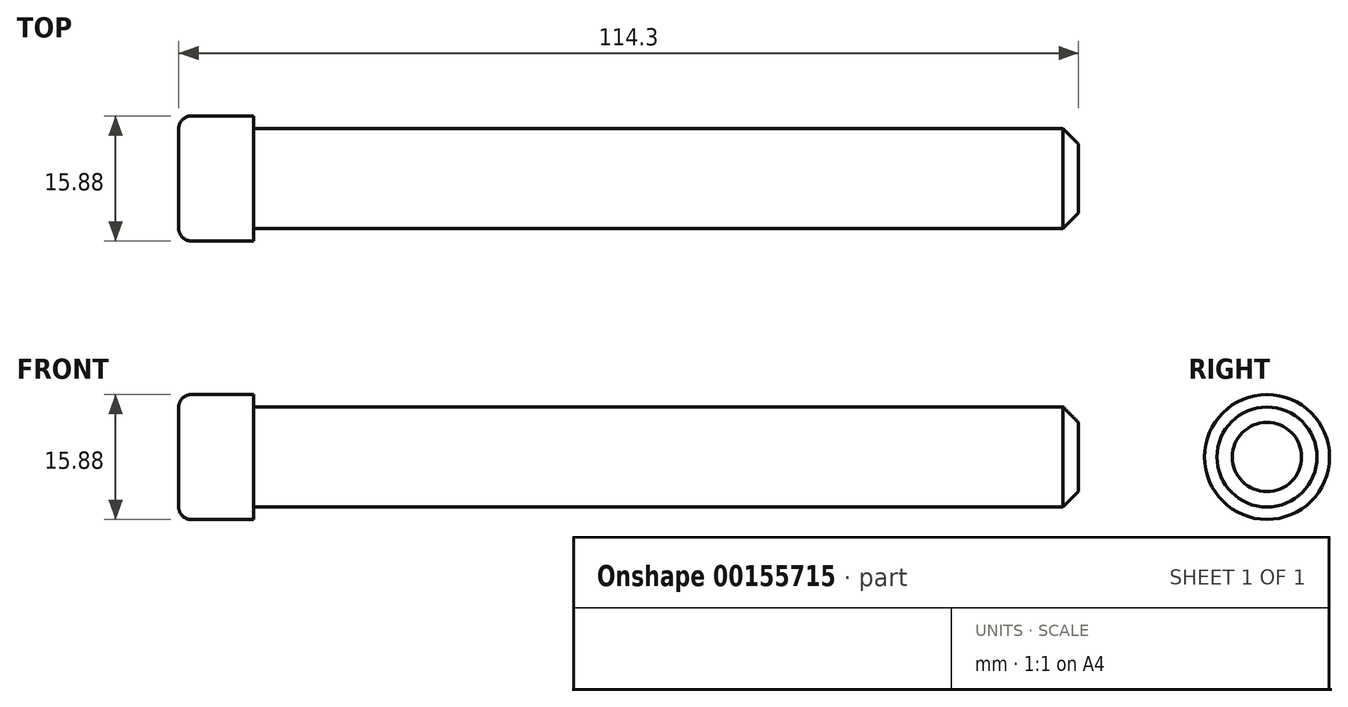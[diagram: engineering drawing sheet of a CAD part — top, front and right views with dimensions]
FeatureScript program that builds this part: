
annotation { "Feature Type Name" : "Feature", "Feature Type Description" : "" }
export const myFeature = defineFeature(function(context is Context, id is Id, definition is map)
    precondition{}
    {
        {
            var Q0;
            Q0=qCreatedBy(makeId("Front.planeOp"),FACE);
            var sketch = newSketch(context, id + "F1", { "sketchPlane" : qUnion([Q0])});
            skLineSegment(sketch, "E0.bottom", {"start": v(-55.56, 7.94) * mm, "end": v(-47.62, 7.94) * mm});
            skLineSegment(sketch, "E0.top", {"start": v(-57.15, 0) * mm, "end": v(57.15, 0) * mm});
            skLineSegment(sketch, "E0.left", {"start": v(-57.15, 6.35) * mm, "end": v(-57.15, 0) * mm});
            skLineSegment(sketch, "E0.right", {"start": v(57.15, 4.4) * mm, "end": v(57.15, 0) * mm});
            skLineSegment(sketch, "E1", {"start": v(55.2, 6.35) * mm, "end": v(-47.63, 6.35) * mm});
            skLineSegment(sketch, "E2", {"start": v(-47.62, 6.35) * mm, "end": v(-47.62, 7.94) * mm});
            skPoint(sketch, "E3.visualSharp", {"position": v(-57.15, 7.94) * mm});
            skArc(sketch, "E3.filletArc", {"start": v(-55.56, 7.94) * mm, "mid": v(-56.69, 7.47) * mm, "end": v(-57.15, 6.35) * mm});
            skLineSegment(sketch, "E4", {"start": v(57.15, 4.4) * mm, "end": v(55.2, 6.35) * mm});
            skSolve(sketch);
        }
        {
            var Q0;
            Q0 = qSketchRegion(id + "F1", true);
            var Q1;
            Q1=sQuery(id+"F1.wireOp",EDGE,"E0.top");
            revolve(context, id + "F0", {"entities" : qUnion([Q0]), "axis" : qUnion([Q1]), "revolveType" : RevolveType.FULL});
        }
    });
